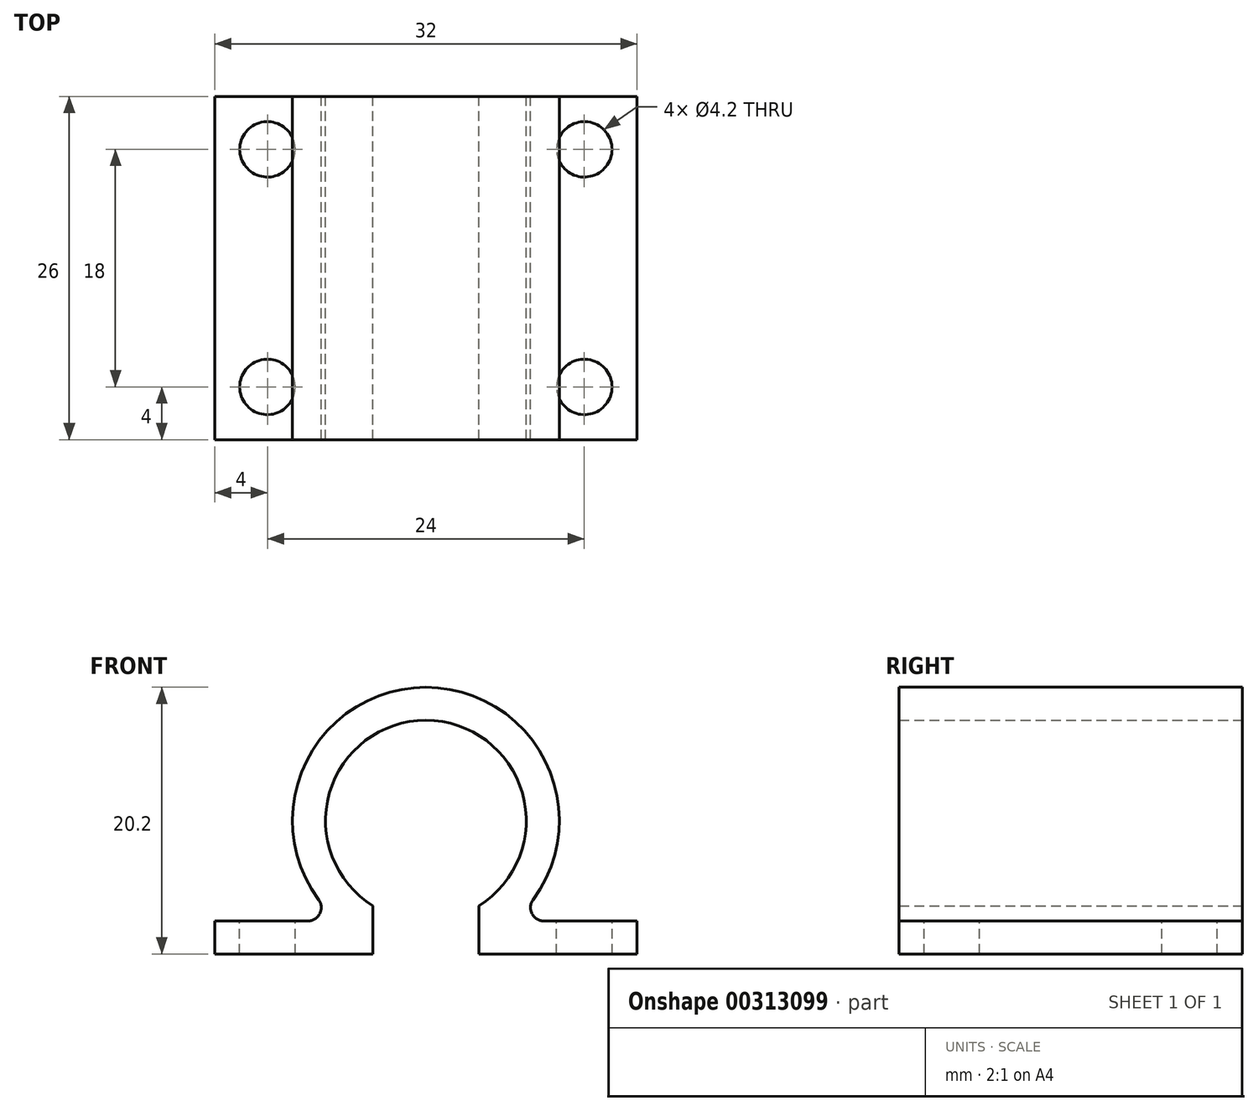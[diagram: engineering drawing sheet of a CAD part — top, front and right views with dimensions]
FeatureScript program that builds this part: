
annotation { "Feature Type Name" : "Feature", "Feature Type Description" : "" }
export const myFeature = defineFeature(function(context is Context, id is Id, definition is map)
    precondition{}
    {
        {
            var Q0;
            Q0=qCreatedBy(makeId("Front.planeOp"),FACE);
            var sketch = newSketch(context, id + "F0", { "sketchPlane" : qUnion([Q0])});
            skLineSegment(sketch, "E0", {"start": v(0, 0) * mm, "end": v(-4, 0) * mm, "construction": true});
            skLineSegment(sketch, "E1", {"start": v(0, 0) * mm, "end": v(4, 0) * mm, "construction": true});
            skLineSegment(sketch, "E2", {"start": v(-16, 0) * mm, "end": v(-16, 2.5) * mm});
            skLineSegment(sketch, "E3", {"start": v(-16, 2.5) * mm, "end": v(-8.92, 2.5) * mm});
            skLineSegment(sketch, "E4", {"start": v(16, 2.5) * mm, "end": v(16, 0) * mm});
            skLineSegment(sketch, "E5.trimOffspring", {"start": v(8.92, 2.5) * mm, "end": v(16, 2.5) * mm});
            skArc(sketch, "E6", {"start": v(8.12, 4.1) * mm, "mid": v(0, 20.2) * mm, "end": v(-8.12, 4.1) * mm});
            skLineSegment(sketch, "E7", {"start": v(-4, 0) * mm, "end": v(-4, 3.64) * mm});
            skLineSegment(sketch, "E8", {"start": v(4, 0) * mm, "end": v(4, 3.64) * mm});
            skArc(sketch, "E9", {"start": v(-4, 3.64) * mm, "mid": v(0, 2.5) * mm, "end": v(4, 3.64) * mm, "construction": true});
            skArc(sketch, "E10", {"start": v(4, 3.64) * mm, "mid": v(0, 17.7) * mm, "end": v(-4, 3.64) * mm});
            skLineSegment(sketch, "E11", {"start": v(-4, 0) * mm, "end": v(-16, 0) * mm});
            skLineSegment(sketch, "E12", {"start": v(4, 0) * mm, "end": v(16, 0) * mm});
            skPoint(sketch, "E13.visualSharp", {"position": v(-6.65, 2.5) * mm});
            skArc(sketch, "E13.filletArc", {"start": v(-8.92, 2.5) * mm, "mid": v(-8.03, 3.05) * mm, "end": v(-8.12, 4.1) * mm});
            skPoint(sketch, "E14.visualSharp", {"position": v(6.65, 2.5) * mm});
            skArc(sketch, "E14.filletArc", {"start": v(8.12, 4.1) * mm, "mid": v(8.03, 3.05) * mm, "end": v(8.92, 2.5) * mm});
            skSolve(sketch);
        }
        {
            var Q0;
            Q0 = qSketchRegion(id + "F0", true);
            extrude(context, id + "F1", {"entities" : qUnion([Q0]), "depth" : 26 * mm});
        }
        {
            var Q0;
            Q0=makeQuery(id+"F1.opExtrude","SWEPT_FACE",FACE,{"disambiguationData":[OSD([sQuery(id+"F0.wireOp",EDGE,"E3")])]});
            var sketch = newSketch(context, id + "F2", { "sketchPlane" : qUnion([Q0])});
            skCircle(sketch, "E15", {"center": v(-12, -22) * mm, "radius": 2.1 * mm});
            skCircle(sketch, "E16", {"center": v(-12, -4) * mm, "radius": 2.1 * mm});
            skCircle(sketch, "E17", {"center": v(12, -22) * mm, "radius": 2.1 * mm});
            skCircle(sketch, "E18", {"center": v(12, -4) * mm, "radius": 2.1 * mm});
            skLineSegment(sketch, "E19", {"start": v(-12, -22) * mm, "end": v(-12, -26) * mm, "construction": true});
            skPoint(sketch, "E19.endSnap0", {"position": v(-12.46, -26) * mm});
            skLineSegment(sketch, "E20", {"start": v(-12, -4) * mm, "end": v(-12, 0) * mm, "construction": true});
            skSolve(sketch);
        }
        {
            var Q0;
            Q0 = qSketchRegion(id + "F2", true);
            extrude(context, id + "F3", {"entities" : qUnion([Q0]), "operationType" : NewBodyOperationType.REMOVE, "endBound" : BoundingType.UP_TO_NEXT, "oppositeDirection" : true, "depth" : 25 * mm});
        }
    });
